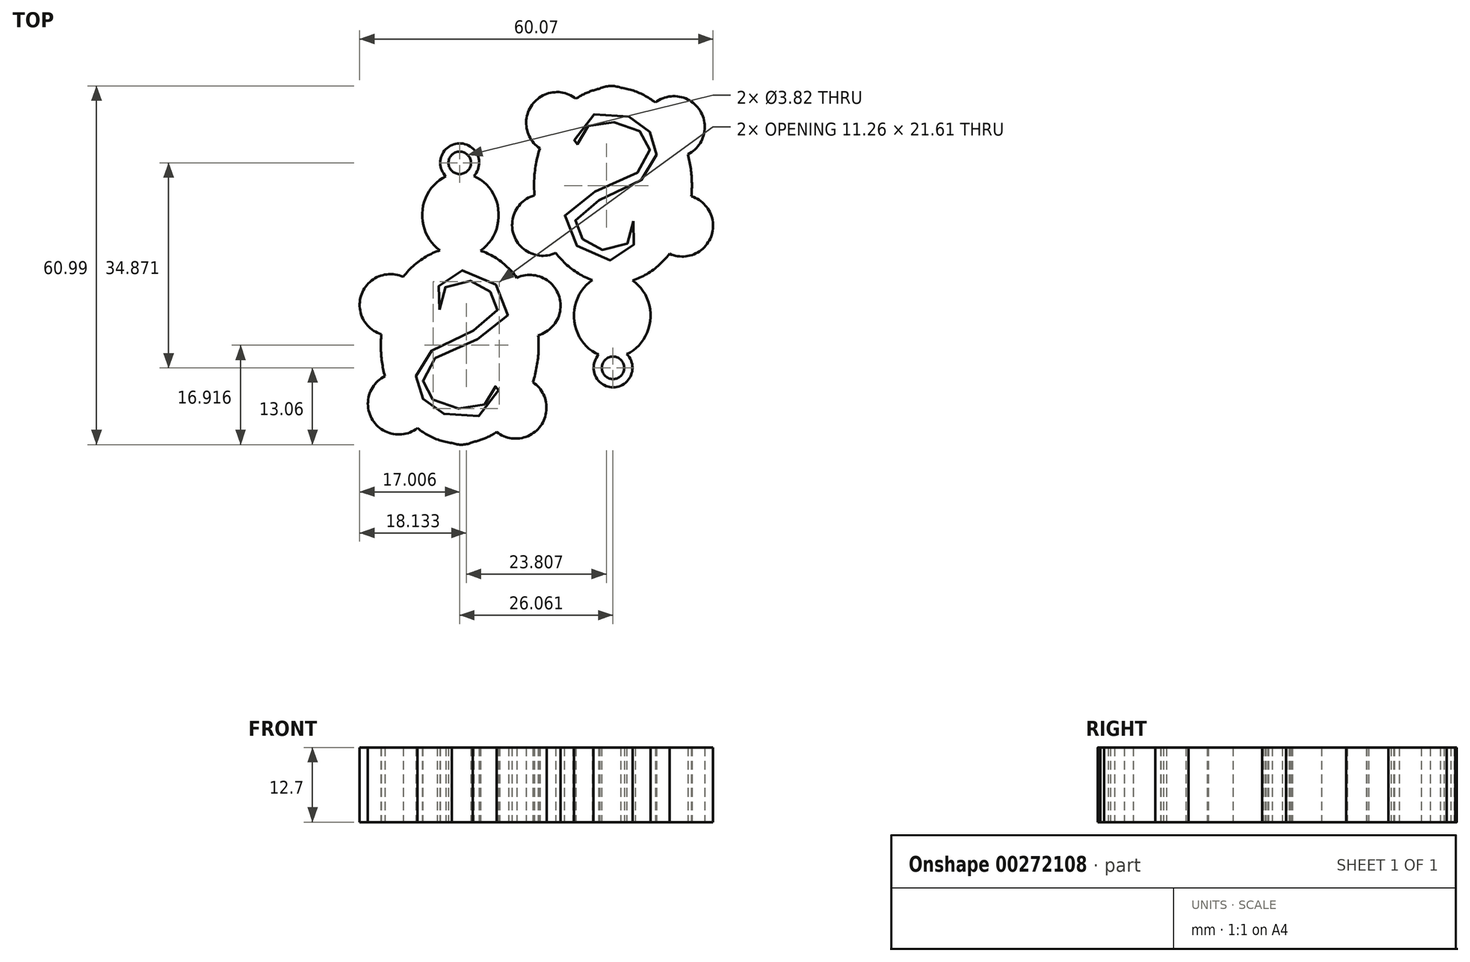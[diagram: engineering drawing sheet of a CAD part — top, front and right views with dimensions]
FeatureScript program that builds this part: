
annotation { "Feature Type Name" : "Feature", "Feature Type Description" : "" }
export const myFeature = defineFeature(function(context is Context, id is Id, definition is map)
    precondition{}
    {
        {
            var Q0;
            Q0=qCreatedBy(makeId("Top.planeOp"),FACE);
            var sketch = newSketch(context, id + "F0", { "sketchPlane" : qUnion([Q0])});
            skArc(sketch, "E0", {"start": v(-42.46, 52.57) * mm, "mid": v(-49.93, 51.53) * mm, "end": v(-48.6, 44.1) * mm});
            skEllipticalArc(sketch, "E1", {});
            skArc(sketch, "E2", {"start": v(-49.51, 36.12) * mm, "mid": v(-52.99, 29.27) * mm, "end": v(-45.9, 26.33) * mm});
            skArc(sketch, "E3", {"start": v(-26.55, 26.2) * mm, "mid": v(-19.5, 29.1) * mm, "end": v(-22.84, 35.96) * mm});
            skArc(sketch, "E4", {"start": v(-23.44, 43.09) * mm, "mid": v(-21.41, 50.62) * mm, "end": v(-29.13, 51.8) * mm});
            skEllipticalArc(sketch, "E5", {});
            skArc(sketch, "E6", {"start": v(-34.85, 54.44) * mm, "mid": v(-36.64, 54.72) * mm, "end": v(-38.4, 54.29) * mm});
            skEllipticalArc(sketch, "E7.trimOffspring", {});
            skEllipticalArc(sketch, "E8.trimOffspring", {});
            skEllipticalArc(sketch, "E9.trimOffspring", {});
            skEllipticalArc(sketch, "E10.trimOffspring", {});
            skEllipticalArc(sketch, "E11.trimOffspring", {});
            skArc(sketch, "E12", {"start": v(-38.58, 9.04) * mm, "mid": v(-36.1, 3.49) * mm, "end": v(-33.82, 9.12) * mm});
            skCircle(sketch, "E13.0", {"center": v(-36.16, 6.8) * mm, "radius": 1.91 * mm});
            skEllipticalArc(sketch, "E14.trimOffspring", {});
            skEllipticalArc(sketch, "E15.trimOffspring", {});
            skFitSpline(sketch, "E16", {"points": [v(-32.72, 31.76) * mm, v(-34.12, 27.38) * mm, v(-39.83, 27.57) * mm, v(-41.9, 29.53) * mm, v(-42.09, 33) * mm, v(-29.83, 39.98) * mm, v(-29.27, 45.45) * mm, v(-31.67, 48.62) * mm, v(-40.4, 49.3) * mm, v(-42.92, 44.03) * mm, v(-41.77, 45.7) * mm, v(-39.67, 48.35) * mm, v(-32.84, 47.79) * mm, v(-30.33, 45.24) * mm, v(-30.88, 40.83) * mm, v(-43.98, 33.54) * mm, v(-40.45, 26.15) * mm, v(-32.97, 26.84) * mm, v(-32.72, 31.76) * mm]});
            skArc(sketch, "E17", {"start": v(-55.93, -4.12) * mm, "mid": v(-48.46, -3.08) * mm, "end": v(-49.79, 4.35) * mm});
            skEllipticalArc(sketch, "E18", {});
            skArc(sketch, "E19", {"start": v(-48.88, 12.33) * mm, "mid": v(-45.4, 19.18) * mm, "end": v(-52.5, 22.12) * mm});
            skArc(sketch, "E20", {"start": v(-71.83, 22.26) * mm, "mid": v(-78.89, 19.35) * mm, "end": v(-75.54, 12.5) * mm});
            skArc(sketch, "E21", {"start": v(-74.94, 5.36) * mm, "mid": v(-76.97, -2.17) * mm, "end": v(-69.26, -3.35) * mm});
            skEllipticalArc(sketch, "E22", {});
            skArc(sketch, "E23", {"start": v(-63.54, -5.99) * mm, "mid": v(-61.74, -6.27) * mm, "end": v(-59.98, -5.84) * mm});
            skEllipticalArc(sketch, "E24.trimOffspring", {});
            skEllipticalArc(sketch, "E25.trimOffspring", {});
            skEllipticalArc(sketch, "E26.trimOffspring", {});
            skEllipticalArc(sketch, "E27.trimOffspring", {});
            skEllipticalArc(sketch, "E28.trimOffspring", {});
            skArc(sketch, "E29", {"start": v(-59.8, 39.41) * mm, "mid": v(-62.28, 44.96) * mm, "end": v(-64.57, 39.33) * mm});
            skCircle(sketch, "E30.0", {"center": v(-62.22, 41.66) * mm, "radius": 1.91 * mm});
            skEllipticalArc(sketch, "E31.trimOffspring", {});
            skEllipticalArc(sketch, "E32.trimOffspring", {});
            skFitSpline(sketch, "E33", {"points": [v(-65.67, 16.69) * mm, v(-64.26, 21.08) * mm, v(-58.55, 20.88) * mm, v(-56.49, 18.92) * mm, v(-56.3, 15.45) * mm, v(-68.55, 8.47) * mm, v(-69.11, 3) * mm, v(-66.71, -0.17) * mm, v(-57.98, -0.86) * mm, v(-55.46, 4.42) * mm, v(-56.62, 2.74) * mm, v(-58.71, 0.1) * mm, v(-65.55, 0.67) * mm, v(-68.06, 3.2) * mm, v(-67.5, 7.62) * mm, v(-54.4, 14.9) * mm, v(-57.94, 22.3) * mm, v(-65.42, 21.6) * mm, v(-65.67, 16.69) * mm]});
            const initialGuessF0  = {"E1": [-0.03629690936040839, 0.0156749826480331, 0, -1, 0.007088771999557837, 0.006498040999594687, 3.6910871090156703, 5.923609683701958], "E5": [-0.03616955464705143, 0.03782710589874991, 0, -1, 0.016692501233453734, 0.013410738515496906, 3.3089592846980826, 3.62942529102692], "E7.trimOffspring": [-0.03616955464705143, 0.03782710589874991, 0, -1, 0.016692501233453734, 0.013410738515496906, 0.2524372803543637, 0.7994791178705879], "E8.trimOffspring": [-0.03616955464705143, 0.03782710589874991, 0, -1, 0.016692501233453734, 0.013410738515496906, 4.32692058638585, 4.814724216336093], "E9.trimOffspring": [-0.03616955464705143, 0.03782710589874991, 0, -1, 0.016692501233453734, 0.013410738515496906, 2.575662651388378, 3.0429824637441554], "E10.trimOffspring": [-0.03616955464705143, 0.03782710589874991, 0, -1, 0.016692501233453734, 0.013410738515496906, 1.4585950026837142, 1.8912942522877056], "E11.trimOffspring": [-0.03616955464705143, 0.03782710589874991, 0, -1, 0.016692501233453734, 0.013410738515496906, 5.472109223511273, 6.017520772851198], "E14.trimOffspring": [-0.03629690936040839, 0.0156749826480331, 0, -1, 0.007088771999557837, 0.006498040999594687, 0.39107533446163945, 2.5770061583371633], "E15.trimOffspring": [-0.03629690936040839, 0.0156749826480331, 0, -1, 0.007088771999557837, 0.006498040999594687, 6.211281138852462, 0.10370611853058007], "E18": [-0.06208908616775573, 0.03277564247812973, 0, 1, 0.007088771999557663, 0.006498040999594843, 3.691087109015656, 5.923609683701975], "E22": [-0.06221644088111271, 0.010623519227413017, 0, 1, 0.016692501233453734, 0.013410738515496906, 3.3089592846980844, 3.629425291026912], "E24.trimOffspring": [-0.06221644088111271, 0.010623519227413017, 0, 1, 0.016692501233453734, 0.013410738515496906, 0.2524372803543671, 0.7994791178705936], "E25.trimOffspring": [-0.06221644088111271, 0.010623519227413017, 0, 1, 0.016692501233453734, 0.013410738515496906, 4.326920586385848, 4.814724216336087], "E26.trimOffspring": [-0.062216440881112715, 0.010623519227413017, 0, 1, 0.016692501233453734, 0.013410738515496906, 2.5756626513883867, 3.042982463744158], "E27.trimOffspring": [-0.06221644088111271, 0.010623519227413017, 0, 1, 0.016692501233453734, 0.013410738515496906, 1.4585950026837202, 1.891294252287709], "E28.trimOffspring": [-0.06221644088111271, 0.010623519227413017, 0, 1, 0.016692501233453734, 0.013410738515496906, 5.472109223511268, 6.017520772851196], "E31.trimOffspring": [-0.062089086167755735, 0.03277564247812973, 0, 1, 0.007088771999557663, 0.006498040999594843, 0.3910753344616232, 2.5770061583371744], "E32.trimOffspring": [-0.06208908616775573, 0.03277564247812973, 0, 1, 0.007088771999557663, 0.006498040999594843, 6.211281138852467, 0.1037061185305769]};
            skSetInitialGuess(sketch, initialGuessF0);
            skSolve(sketch);
        }
        {
            var Q0;
            Q0 = qSketchRegion(id + "F0", true);
            extrude(context, id + "F1", {"entities" : qUnion([Q0]), "depth" : 12.7 * mm});
        }
    });
